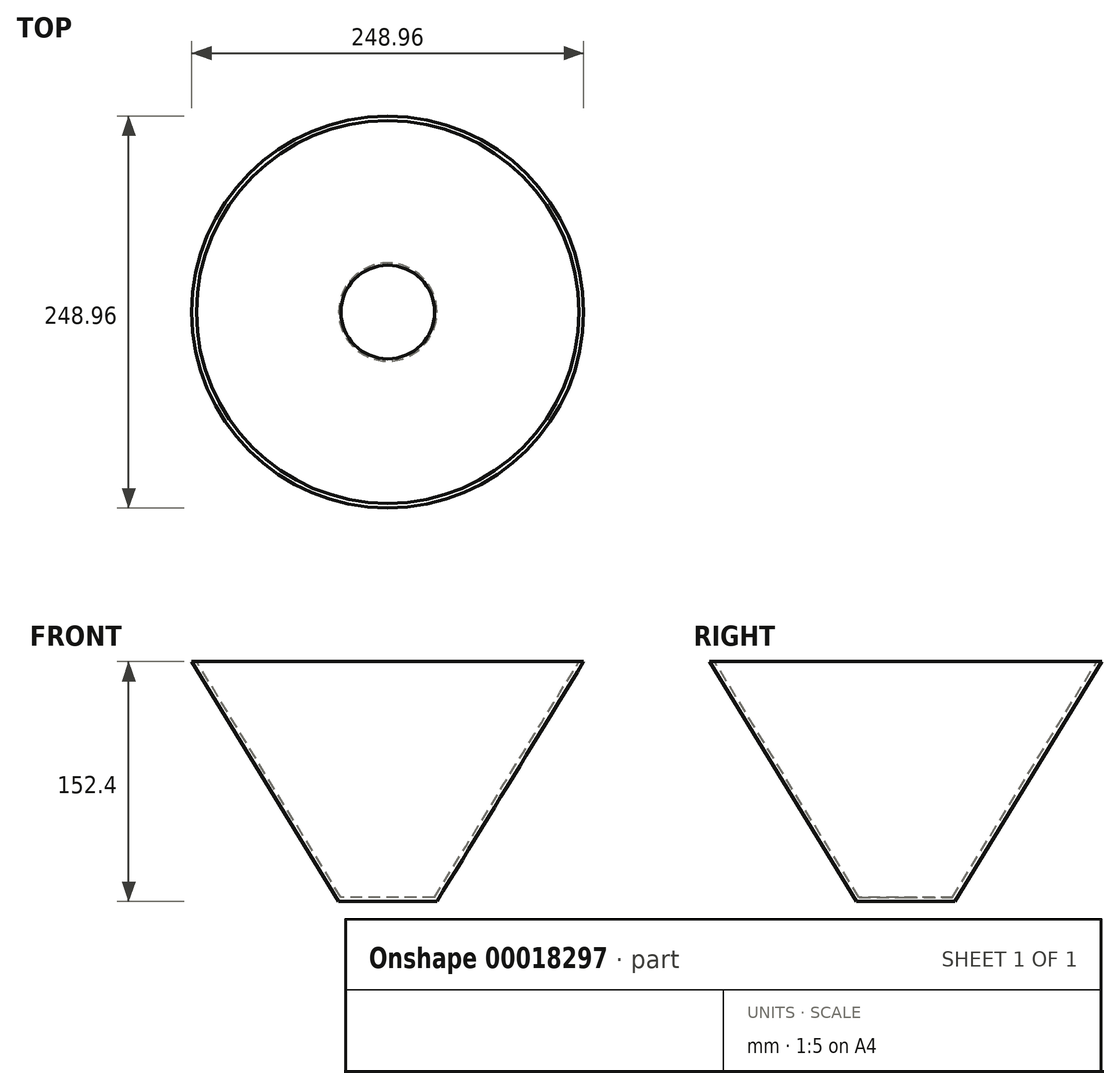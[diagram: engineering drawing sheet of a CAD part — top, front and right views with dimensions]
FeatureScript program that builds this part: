
annotation { "Feature Type Name" : "Feature", "Feature Type Description" : "" }
export const myFeature = defineFeature(function(context is Context, id is Id, definition is map)
    precondition{}
    {
        {
            var Q0;
            Q0=qCreatedBy(makeId("Top.planeOp"),FACE);
            var sketch = newSketch(context, id + "F0", { "sketchPlane" : qUnion([Q0])});
            skCircle(sketch, "E0", {"center": v(0, 0) * mm, "radius": 31.16 * mm});
            skSolve(sketch);
        }
        {
            var Q0;
            Q0=makeQuery(id+"F0.imprint","IMPRINT",FACE,{"disambiguationData":[TD([[makeQuery(id+"F0.imprint","IMPRINT",EDGE,{"derivedFrom":sQuery(id+"F0.wireOp",EDGE,"E0")}),1.0]])]});
            cPlane(context, id + "F1", {"entities" : qUnion([Q0]), "cplaneType" : CPlaneType.OFFSET, "offset" : 152.4 * mm, "width" : 152.4 * mm, "height" : 152.4 * mm});
        }
        {
            var Q0;
            Q0=qCreatedBy(id+"F1.planeOp",FACE);
            var sketch = newSketch(context, id + "F2", { "sketchPlane" : qUnion([Q0])});
            skPoint(sketch, "E1.0", {"position": v(0, 0) * mm});
            skCircle(sketch, "E2", {"center": v(0, 0) * mm, "radius": 124.48 * mm});
            skSolve(sketch);
        }
        {
            var Q0;
            Q0=makeQuery(id+"F2.imprint","IMPRINT",FACE,{"disambiguationData":[TD([[makeQuery(id+"F2.imprint","IMPRINT",EDGE,{"derivedFrom":sQuery(id+"F2.wireOp",EDGE,"E2")}),1.0]])]});
            var Q1;
            Q1=makeQuery(id+"F0.imprint","IMPRINT",FACE,{"disambiguationData":[TD([[makeQuery(id+"F0.imprint","IMPRINT",EDGE,{"derivedFrom":sQuery(id+"F0.wireOp",EDGE,"E0")}),1.0]])]});
            loft(context, id + "F3", {"sheetProfilesArray" : [{ "sheetProfileEntities" : qUnion([Q0]) }, { "sheetProfileEntities" : qUnion([Q1]) }]});
        }
        {
            var Q0;
            Q0=makeQuery(id+"F3.opLoft","CAP_FACE",FACE,{"disambiguationData":[OSD([makeQuery(id+"F2.imprint","IMPRINT",FACE,{"disambiguationData":[TD([[makeQuery(id+"F2.imprint","IMPRINT",EDGE,{"derivedFrom":sQuery(id+"F2.wireOp",EDGE,"E2")}),1.0]])]})])],"isStart":true});
            var Q1;
            Q1=makeQuery(id+"F3.opLoft","SWEPT_BODY",BODY,{"disambiguationData":[OSD([makeQuery(id+"F0.imprint","IMPRINT",FACE,{"disambiguationData":[TD([[makeQuery(id+"F0.imprint","IMPRINT",EDGE,{"derivedFrom":sQuery(id+"F0.wireOp",EDGE,"E0")}),1.0]])]}),makeQuery(id+"F2.imprint","IMPRINT",FACE,{"disambiguationData":[TD([[makeQuery(id+"F2.imprint","IMPRINT",EDGE,{"derivedFrom":sQuery(id+"F2.wireOp",EDGE,"E2")}),1.0]])]})])]});
            shell(context, id + "F4", {"entities" : qUnion([Q0]), "parts" : qUnion([Q1]), "thickness" : 2.54 * mm});
        }
        {
            var Q0;
            Q0=qCreatedBy(makeId("Front.planeOp"),FACE);
            cPlane(context, id + "F5", {"entities" : qUnion([Q0]), "cplaneType" : CPlaneType.OFFSET, "offset" : 76.2 * mm, "width" : 152.4 * mm, "height" : 152.4 * mm});
        }
        {
            var Q0;
            Q0=qCreatedBy(makeId("Right.planeOp"),FACE);
            cPlane(context, id + "F6", {"entities" : qUnion([Q0]), "cplaneType" : CPlaneType.OFFSET, "offset" : 76.2 * mm, "width" : 152.4 * mm, "height" : 152.4 * mm});
        }
        {
            var Q0;
            Q0=qCreatedBy(id+"F6.planeOp",FACE);
            var sketch = newSketch(context, id + "F7", { "sketchPlane" : qUnion([Q0])});
            skFitSpline(sketch, "E3", {"points": [v(-53.96, 31.63) * mm, v(20, 35.94) * mm, v(45.56, -32) * mm, v(-24.22, -5.13) * mm, v(-40.4, -56.13) * mm, v(-57.39, 8.3) * mm, v(-57.36, 8.55) * mm], "startDerivative": vector(383.18, 162.58) * mm, "endDerivative": vector(5.89, 3.56) * mm});
            skFitSpline(sketch, "E4", {"points": [v(-57.36, 8.55) * mm, v(-54.02, 8.55) * mm], "startDerivative": vector(3.34, 0) * mm, "endDerivative": vector(3.34, 0) * mm});
            skSolve(sketch);
        }
    });
